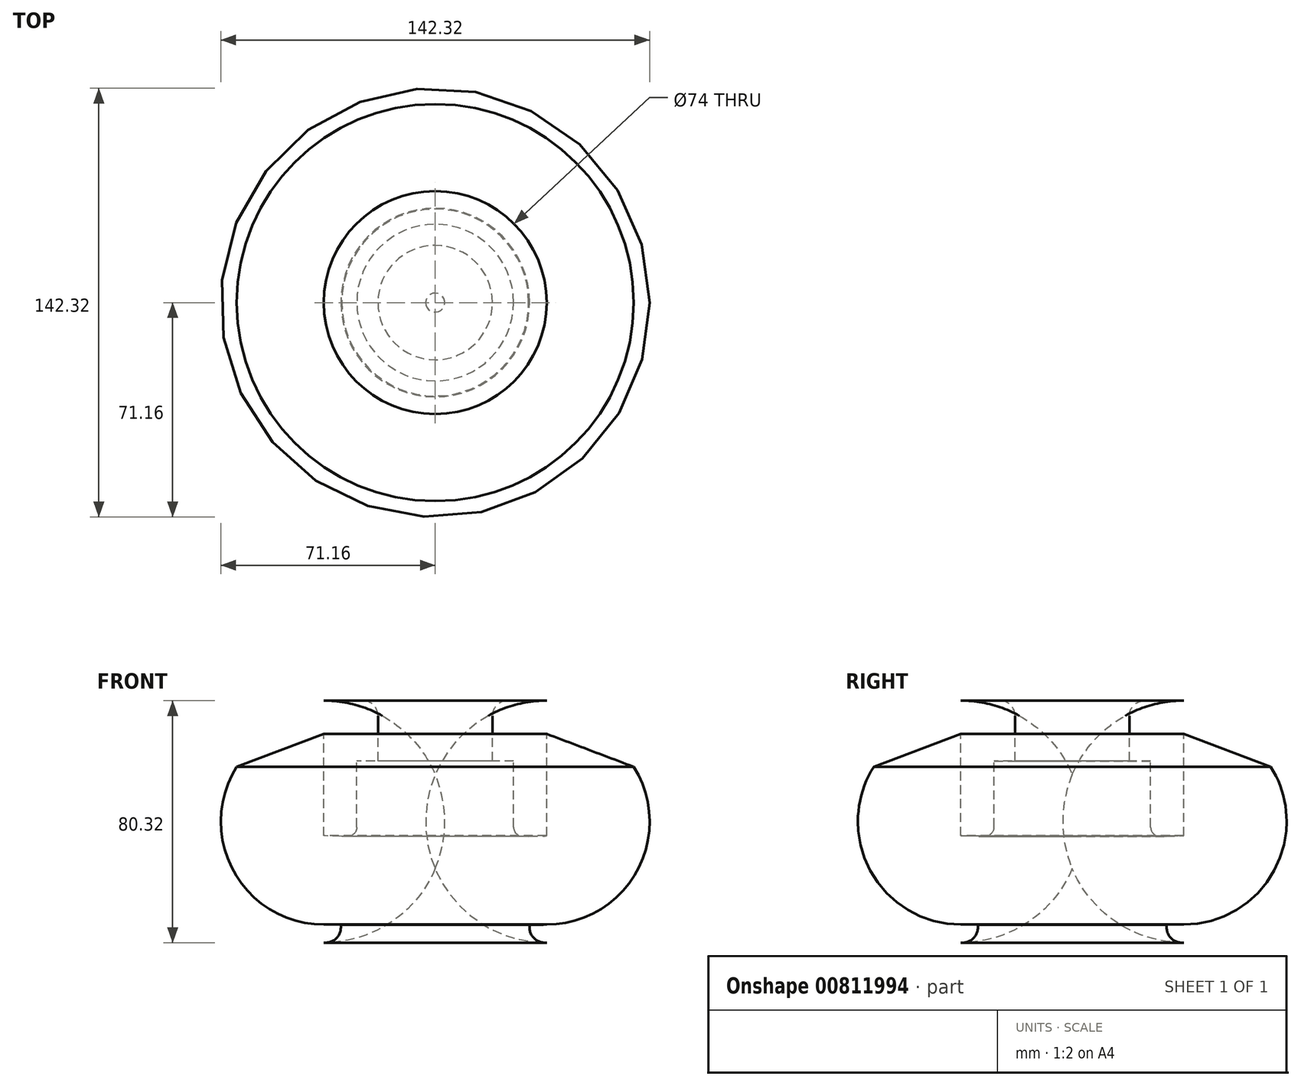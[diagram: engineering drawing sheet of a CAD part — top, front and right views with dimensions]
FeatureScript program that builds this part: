
annotation { "Feature Type Name" : "Feature", "Feature Type Description" : "" }
export const myFeature = defineFeature(function(context is Context, id is Id, definition is map)
    precondition{}
    {
        {
            var Q0;
            Q0=qCreatedBy(makeId("Front.planeOp"),FACE);
            var sketch = newSketch(context, id + "F0", { "sketchPlane" : qUnion([Q0])});
            skLineSegment(sketch, "E0", {"start": v(0, 79.23) * mm, "end": v(0, -3.35) * mm, "construction": true});
            skLineSegment(sketch, "E1", {"start": v(-26.02, 125.96) * mm, "end": v(-26.02, 150.96) * mm});
            skLineSegment(sketch, "E2", {"start": v(-26.03, 125.96) * mm, "end": v(-31.03, 125.96) * mm});
            skLineSegment(sketch, "E3", {"start": v(-26.03, 150.96) * mm, "end": v(-19, 150.96) * mm});
            skLineSegment(sketch, "E4", {"start": v(-19, 150.96) * mm, "end": v(-19, 170.96) * mm});
            skLineSegment(sketch, "E5", {"start": v(-19, 170.96) * mm, "end": v(-37, 170.96) * mm});
            skPoint(sketch, "E6", {"position": v(-56.54, 125.96) * mm});
            skPoint(sketch, "E7", {"position": v(-56.54, 170.96) * mm});
            skPoint(sketch, "E8.end.orphan", {"position": v(-44.5, 170.96) * mm});
            skPoint(sketch, "E8.start.orphan", {"position": v(-87.06, 125.96) * mm});
            skLineSegment(sketch, "E9", {"start": v(0, 91.03) * mm, "end": v(0, -5.66) * mm, "construction": true});
            skLineSegment(sketch, "E10", {"start": v(-37, 90.64) * mm, "end": v(-37, 90.64) * mm});
            skLineSegment(sketch, "E11", {"start": v(0, -3.35) * mm, "end": v(0, -63.67) * mm, "construction": true});
            skPoint(sketch, "E12.orphan", {"position": v(-65.9, 159.96) * mm});
            skPoint(sketch, "E13.start.orphan", {"position": v(-37, 159.96) * mm});
            skArc(sketch, "E14", {"start": v(-37, 170.96) * mm, "mid": v(-77.16, 130.8) * mm, "end": v(-37, 90.64) * mm});
            skLineSegment(sketch, "E15", {"start": v(-37, 90.64) * mm, "end": v(-31.38, 90.64) * mm});
            skLineSegment(sketch, "E16", {"start": v(-31.32, 96.58) * mm, "end": v(-31.38, 90.64) * mm});
            skArc(sketch, "E17.0", {"start": v(-37, 164.96) * mm, "mid": v(-71.16, 130.8) * mm, "end": v(-37, 96.64) * mm});
            skLineSegment(sketch, "E18", {"start": v(-37, 96.64) * mm, "end": v(-31.32, 96.58) * mm});
            skLineSegment(sketch, "E19", {"start": v(-37, 164.96) * mm, "end": v(-37, 126.1) * mm});
            skLineSegment(sketch, "E20", {"start": v(-37, 126.1) * mm, "end": v(-31.03, 125.96) * mm});
            skLineSegment(sketch, "E21", {"start": v(-37, 159.96) * mm, "end": v(-65.9, 149) * mm});
            skSolve(sketch);
        }
        {
            var Q0;
            Q0 = qSketchRegion(id + "F0", true);
            var Q1;
            Q1=sQuery(id+"F0.wireOp",EDGE,"E9");
            revolve(context, id + "F1", {"surfaceOperationType" : NewSurfaceOperationType.NEW, "entities" : qUnion([Q0]), "axis" : qUnion([Q1]), "revolveType" : RevolveType.FULL});
        }
        {
            var Q0;
            Q0=makeQuery(id+"F1.opRevolve","SWEPT_EDGE",EDGE,{"disambiguationData":[OSD([sQuery(id+"F0.wireOp",EDGE,"E1"),sQuery(id+"F0.wireOp",EDGE,"E2")])]});
            fillet(context, id + "F2", {"entities" : qUnion([Q0]), "radius" : 3 * mm, "tangentPropagation" : true, "allowEdgeOverflow" : false});
        }
        {
            var Q0;
            Q0=makeQuery(id+"F1.opRevolve","SWEPT_EDGE",EDGE,{"disambiguationData":[OSD([sQuery(id+"F0.wireOp",EDGE,"E15"),sQuery(id+"F0.wireOp",EDGE,"E16")])]});
            var Q1;
            Q1=makeQuery(id+"F1.opRevolve","SWEPT_EDGE",EDGE,{"disambiguationData":[OSD([sQuery(id+"F0.wireOp",EDGE,"E4"),sQuery(id+"F0.wireOp",EDGE,"E5")])]});
            fillet(context, id + "F3", {"entities" : qUnion([Q0, Q1]), "radius" : 5 * mm, "tangentPropagation" : true, "allowEdgeOverflow" : false});
        }
    });
